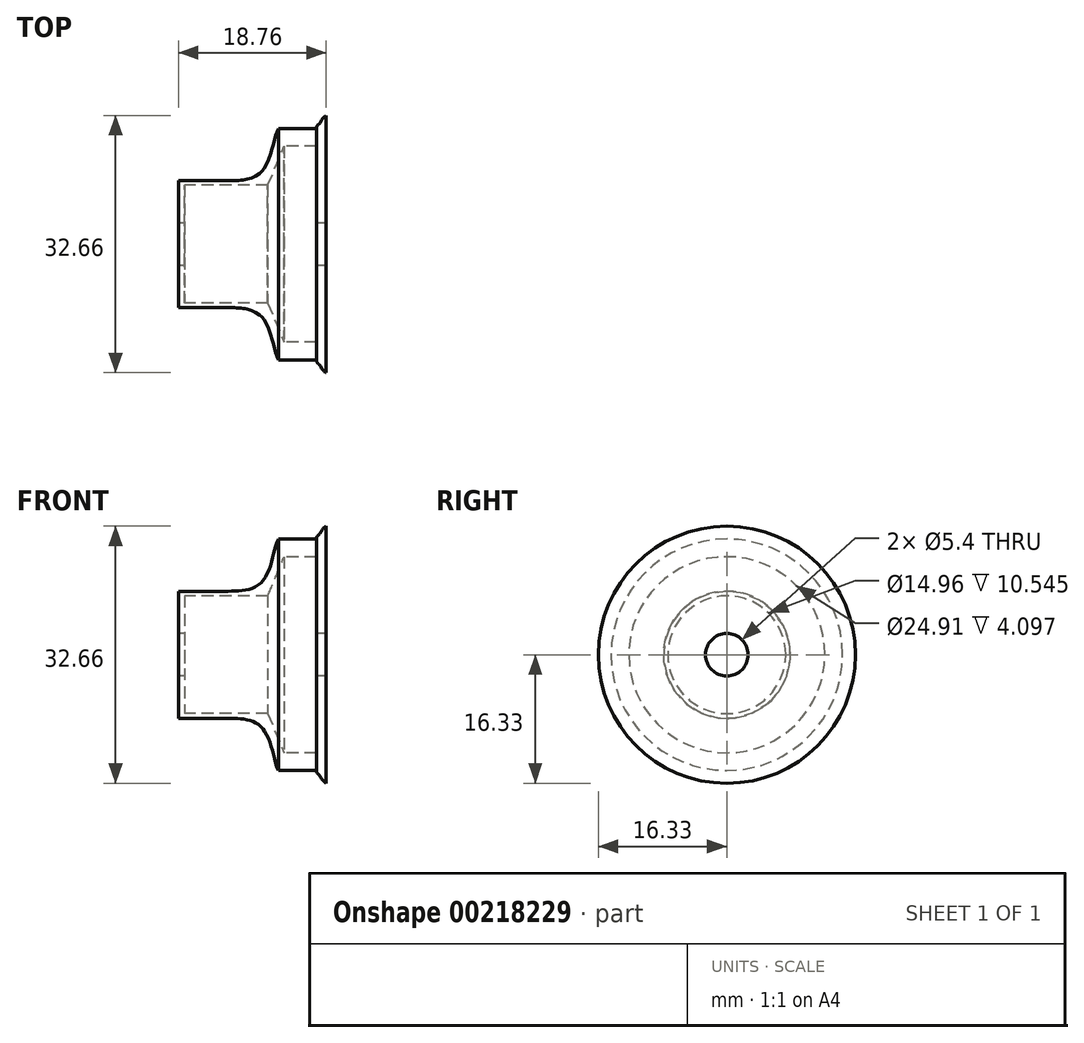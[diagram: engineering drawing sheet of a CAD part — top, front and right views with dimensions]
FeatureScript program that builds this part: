
annotation { "Feature Type Name" : "Feature", "Feature Type Description" : "" }
export const myFeature = defineFeature(function(context is Context, id is Id, definition is map)
    precondition{}
    {
        {
            var Q0;
            Q0=qCreatedBy(makeId("Top.planeOp"),FACE);
            var sketch = newSketch(context, id + "F0", { "sketchPlane" : qUnion([Q0])});
            skLineSegment(sketch, "E0", {"start": v(0, 8.07) * mm, "end": v(6.3, 8.07) * mm});
            skLineSegment(sketch, "E1", {"start": v(12.7, 14.7) * mm, "end": v(17.5, 14.7) * mm});
            skLineSegment(sketch, "E2", {"start": v(18.76, 16.33) * mm, "end": v(18.76, 2.7) * mm});
            skLineSegment(sketch, "E3", {"start": v(18.76, 2.7) * mm, "end": v(17.52, 2.7) * mm});
            skLineSegment(sketch, "E4", {"start": v(0, 2.7) * mm, "end": v(0, 8.07) * mm});
            skLineSegment(sketch, "E5", {"start": v(-2.93, 0) * mm, "end": v(20.9, 0) * mm, "construction": true});
            skFitSpline(sketch, "E6", {"points": [v(12.7, 14.7) * mm, v(10.75, 9.45) * mm, v(6.3, 8.07) * mm], "startDerivative": vector(-3.06, -4.53) * mm, "endDerivative": vector(-9.86, 0.03) * mm});
            skFitSpline(sketch, "E7", {"points": [v(18.76, 16.33) * mm, v(17.9, 15.3) * mm, v(17.5, 14.7) * mm], "startDerivative": vector(-2.77, -1.54) * mm, "endDerivative": vector(-0.33, -3.1) * mm});
            skLineSegment(sketch, "E8", {"start": v(0, 2.7) * mm, "end": v(0.8, 2.7) * mm});
            skLineSegment(sketch, "E9", {"start": v(0.8, 2.7) * mm, "end": v(0.8, 7.48) * mm});
            skLineSegment(sketch, "E10", {"start": v(0.8, 7.48) * mm, "end": v(11.34, 7.48) * mm});
            skLineSegment(sketch, "E11", {"start": v(11.34, 7.48) * mm, "end": v(13.43, 12.45) * mm});
            skLineSegment(sketch, "E12", {"start": v(13.43, 12.45) * mm, "end": v(17.52, 12.45) * mm});
            skLineSegment(sketch, "E13", {"start": v(17.52, 12.45) * mm, "end": v(17.52, 2.7) * mm});
            skLineSegment(sketch, "E14", {"start": v(0.8, 2.7) * mm, "end": v(0, 2.7) * mm});
            skSolve(sketch);
        }
        {
            var Q0;
            Q0=makeQuery(id+"F0.imprint","IMPRINT",FACE,{"disambiguationData":[TD([[makeQuery(id+"F0.imprint","IMPRINT",EDGE,{"derivedFrom":sQuery(id+"F0.wireOp",EDGE,"E0")}),-1.0]])]});
            var Q1;
            Q1=sQuery(id+"F0.wireOp",EDGE,"E5");
            revolve(context, id + "F1", {"entities" : qUnion([Q0]), "axis" : qUnion([Q1]), "revolveType" : RevolveType.FULL});
        }
    });
